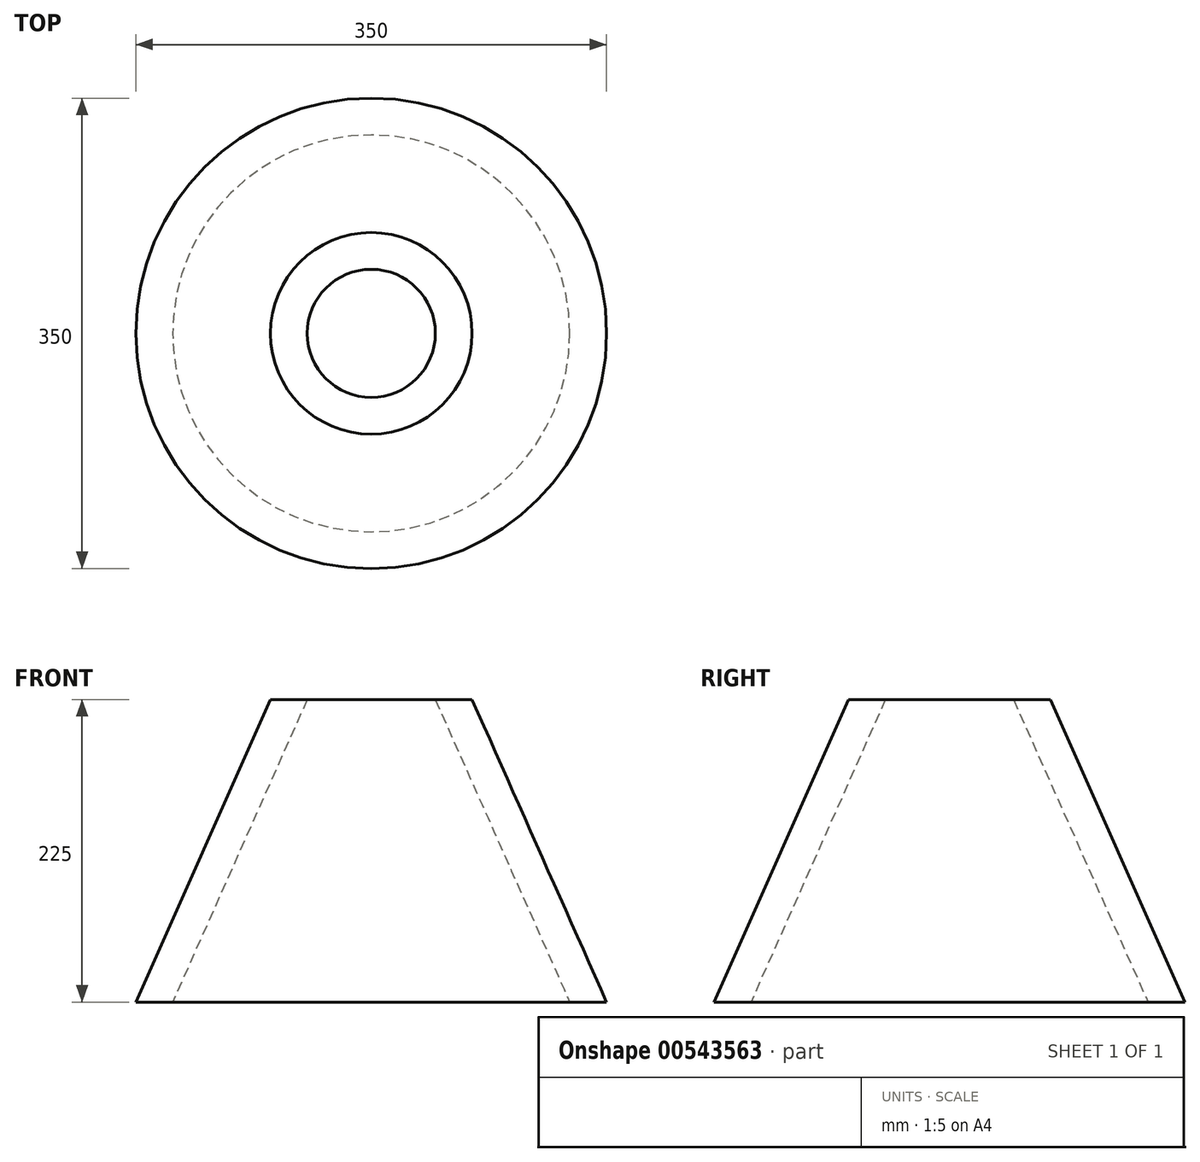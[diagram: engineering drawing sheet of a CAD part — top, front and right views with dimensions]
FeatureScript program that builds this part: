
annotation { "Feature Type Name" : "Feature", "Feature Type Description" : "" }
export const myFeature = defineFeature(function(context is Context, id is Id, definition is map)
    precondition{}
    {
        {
            var Q0;
            Q0=qCreatedBy(makeId("Front.planeOp"),FACE);
            var sketch = newSketch(context, id + "F0", { "sketchPlane" : qUnion([Q0])});
            skLineSegment(sketch, "E0", {"start": v(0, 117.57) * mm, "end": v(0, -107.43) * mm});
            skLineSegment(sketch, "E1", {"start": v(47.64, 117.57) * mm, "end": v(75, 117.57) * mm});
            skLineSegment(sketch, "E2", {"start": v(75, 117.57) * mm, "end": v(175, -107.43) * mm});
            skLineSegment(sketch, "E3", {"start": v(175, -107.43) * mm, "end": v(147.64, -107.43) * mm});
            skLineSegment(sketch, "E4.0", {"start": v(74.84, 117.32) * mm, "end": v(174.77, -107.54) * mm});
            skLineSegment(sketch, "E5.0", {"start": v(47.64, 117.57) * mm, "end": v(147.64, -107.43) * mm});
            skLineSegment(sketch, "E6.0", {"start": v(47.75, 117.32) * mm, "end": v(75, 117.32) * mm});
            skSolve(sketch);
        }
        {
            var Q0;
            Q0 = qSketchRegion(id + "F0", true);
            var Q1;
            Q1=sQuery(id+"F0.wireOp",EDGE,"E0");
            revolve(context, id + "F1", {"entities" : qUnion([Q0]), "axis" : qUnion([Q1]), "revolveType" : RevolveType.FULL});
        }
    });
